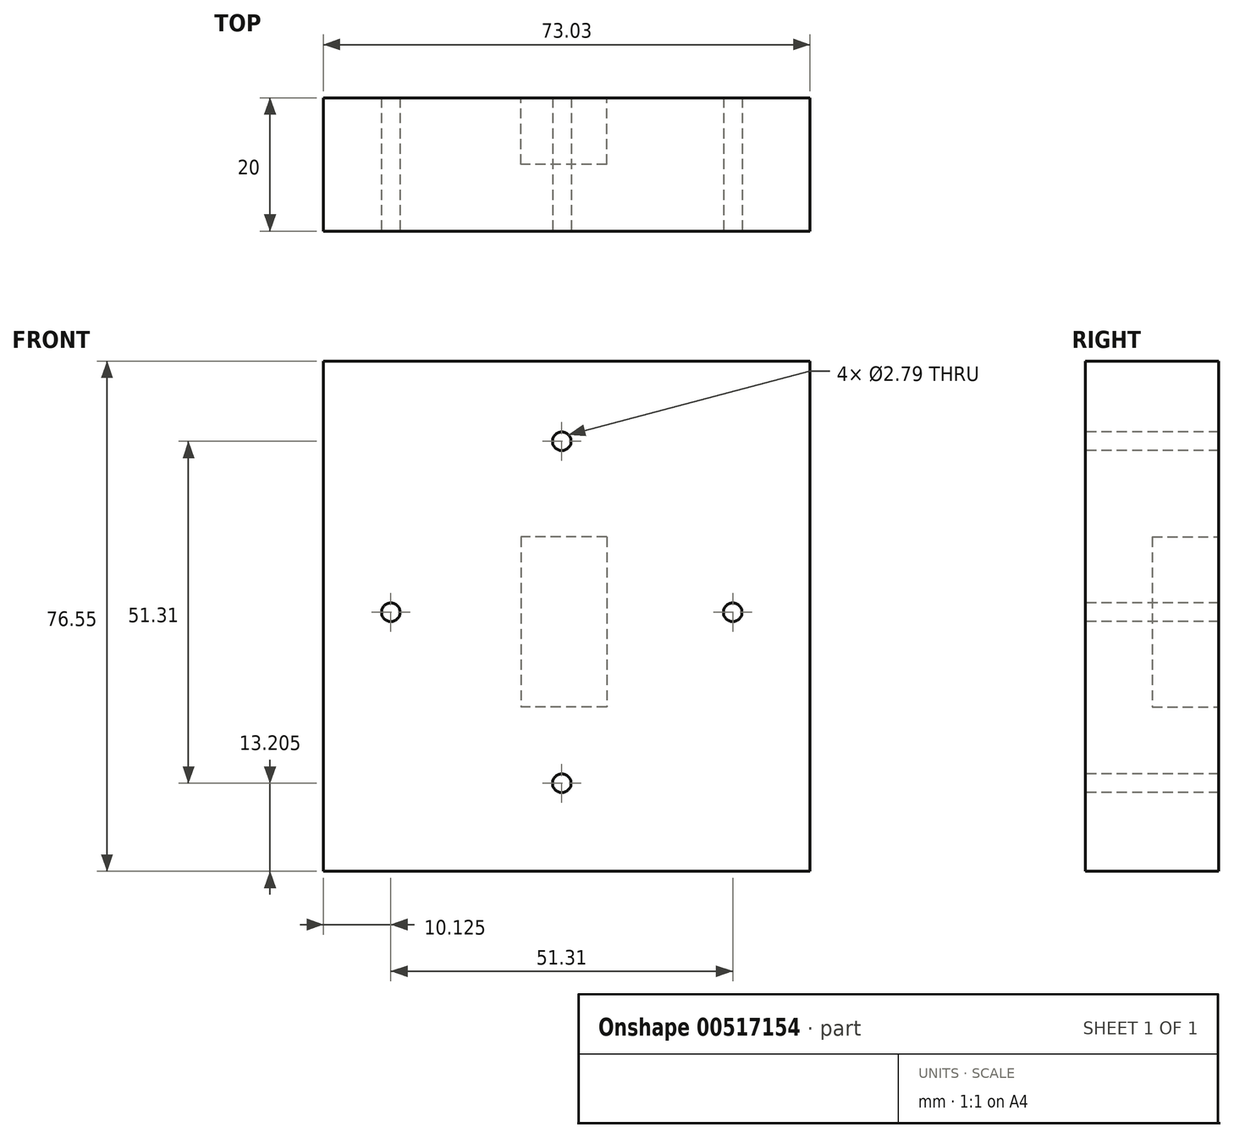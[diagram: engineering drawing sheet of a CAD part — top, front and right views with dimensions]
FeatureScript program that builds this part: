
annotation { "Feature Type Name" : "Feature", "Feature Type Description" : "" }
export const myFeature = defineFeature(function(context is Context, id is Id, definition is map)
    precondition{}
    {
        {
            var Q0;
            Q0=qCreatedBy(makeId("Front.planeOp"),FACE);
            var sketch = newSketch(context, id + "F0", { "sketchPlane" : qUnion([Q0])});
            skLineSegment(sketch, "E0.bottom", {"start": v(-35.78, 37.69) * mm, "end": v(37.25, 37.69) * mm});
            skLineSegment(sketch, "E0.top", {"start": v(-35.78, -38.86) * mm, "end": v(37.25, -38.86) * mm});
            skLineSegment(sketch, "E0.left", {"start": v(-35.78, 37.69) * mm, "end": v(-35.78, -38.86) * mm});
            skLineSegment(sketch, "E0.right", {"start": v(37.25, 37.69) * mm, "end": v(37.25, -38.86) * mm});
            skSolve(sketch);
        }
        {
            var Q0;
            Q0=makeQuery(id+"F0.imprint","IMPRINT",FACE,{"disambiguationData":[TD([[makeQuery(id+"F0.imprint","IMPRINT",EDGE,{"derivedFrom":sQuery(id+"F0.wireOp",EDGE,"E0.bottom")}),-1.0]])]});
            extrude(context, id + "F1", {"entities" : qUnion([Q0]), "depth" : 20 * mm, "offsetDistance" : 25 * mm});
        }
        {
            var Q0;
            Q0=makeQuery(id+"F1.opExtrude","CAP_FACE",FACE,{"disambiguationData":[OSD([sQuery(id+"F0.wireOp",EDGE,"E0.bottom"),sQuery(id+"F0.wireOp",EDGE,"E0.top"),sQuery(id+"F0.wireOp",EDGE,"E0.left"),sQuery(id+"F0.wireOp",EDGE,"E0.right")])],"isStart":true});
            var sketch = newSketch(context, id + "F2", { "sketchPlane" : qUnion([Q0])});
            skLineSegment(sketch, "E1.bottom", {"start": v(-6.75, 11.3) * mm, "end": v(6.16, 11.3) * mm});
            skLineSegment(sketch, "E1.top", {"start": v(-6.75, -14.22) * mm, "end": v(6.16, -14.22) * mm});
            skLineSegment(sketch, "E1.left", {"start": v(-6.75, 11.3) * mm, "end": v(-6.75, -14.22) * mm});
            skLineSegment(sketch, "E1.right", {"start": v(6.16, 11.3) * mm, "end": v(6.16, -14.22) * mm});
            skSolve(sketch);
        }
        {
            var Q0;
            Q0=makeQuery(id+"F2.imprint","IMPRINT",FACE,{"disambiguationData":[TD([[makeQuery(id+"F2.imprint","IMPRINT",EDGE,{"derivedFrom":sQuery(id+"F2.wireOp",EDGE,"E1.bottom")}),-1.0]])]});
            extrude(context, id + "F3", {"entities" : qUnion([Q0]), "operationType" : NewBodyOperationType.REMOVE, "oppositeDirection" : true, "depth" : 10 * mm, "offsetDistance" : 25 * mm});
        }
        {
            var Q0;
            Q0=makeQuery(id+"F1.opExtrude","CAP_FACE",FACE,{"disambiguationData":[OSD([sQuery(id+"F0.wireOp",EDGE,"E0.bottom"),sQuery(id+"F0.wireOp",EDGE,"E0.top"),sQuery(id+"F0.wireOp",EDGE,"E0.left"),sQuery(id+"F0.wireOp",EDGE,"E0.right")])],"isStart":false});
            var sketch = newSketch(context, id + "F4", { "sketchPlane" : qUnion([Q0])});
            skCircle(sketch, "E2", {"center": v(0, 0) * mm, "radius": 25.66 * mm});
            skPoint(sketch, "E3", {"position": v(0, 25.66) * mm});
            skPoint(sketch, "E4", {"position": v(0, -25.66) * mm});
            skPoint(sketch, "E5", {"position": v(25.66, 0) * mm});
            skPoint(sketch, "E6", {"position": v(-25.66, 0) * mm});
            skSolve(sketch);
        }
        {
            var Q0;
            Q0=sQuery(id+"F4.wireOp",VERTEX,"E3");
            var Q1;
            Q1=sQuery(id+"F4.wireOp",VERTEX,"E6");
            var Q2;
            Q2=sQuery(id+"F4.wireOp",VERTEX,"E4");
            var Q3;
            Q3=sQuery(id+"F4.wireOp",VERTEX,"E5");
            var Q4;
            Q4=makeQuery(id+"F1.opExtrude","SWEPT_BODY",BODY,{"disambiguationData":[OSD([sQuery(id+"F0.wireOp",EDGE,"E0.bottom"),sQuery(id+"F0.wireOp",EDGE,"E0.top"),sQuery(id+"F0.wireOp",EDGE,"E0.left"),sQuery(id+"F0.wireOp",EDGE,"E0.right")])]});
            hole(context, id + "F5", {"style" : HoleStyle.SIMPLE, "endStyle" : HoleEndStyle.THROUGH, "standardTappedOrClearance" : lookupTablePath({ "standard" : "ANSI", "fit" : "Normal (ASME)", "size" : "#3", "type" : "Clearance" }), "standardBlindInLast" : lookupTablePath({ "fit" : "Free", "standard" : "ANSI", "size" : "#3", "type" : "Clearance" }), "holeDiameter" : 2.8 * mm, "isTappedThrough" : true, "tappedDepth" : 12.7 * mm, "tapClearance" : 3, "locations" : qUnion([Q0, Q1, Q2, Q3]), "scope" : qUnion([Q4])});
        }
    });
